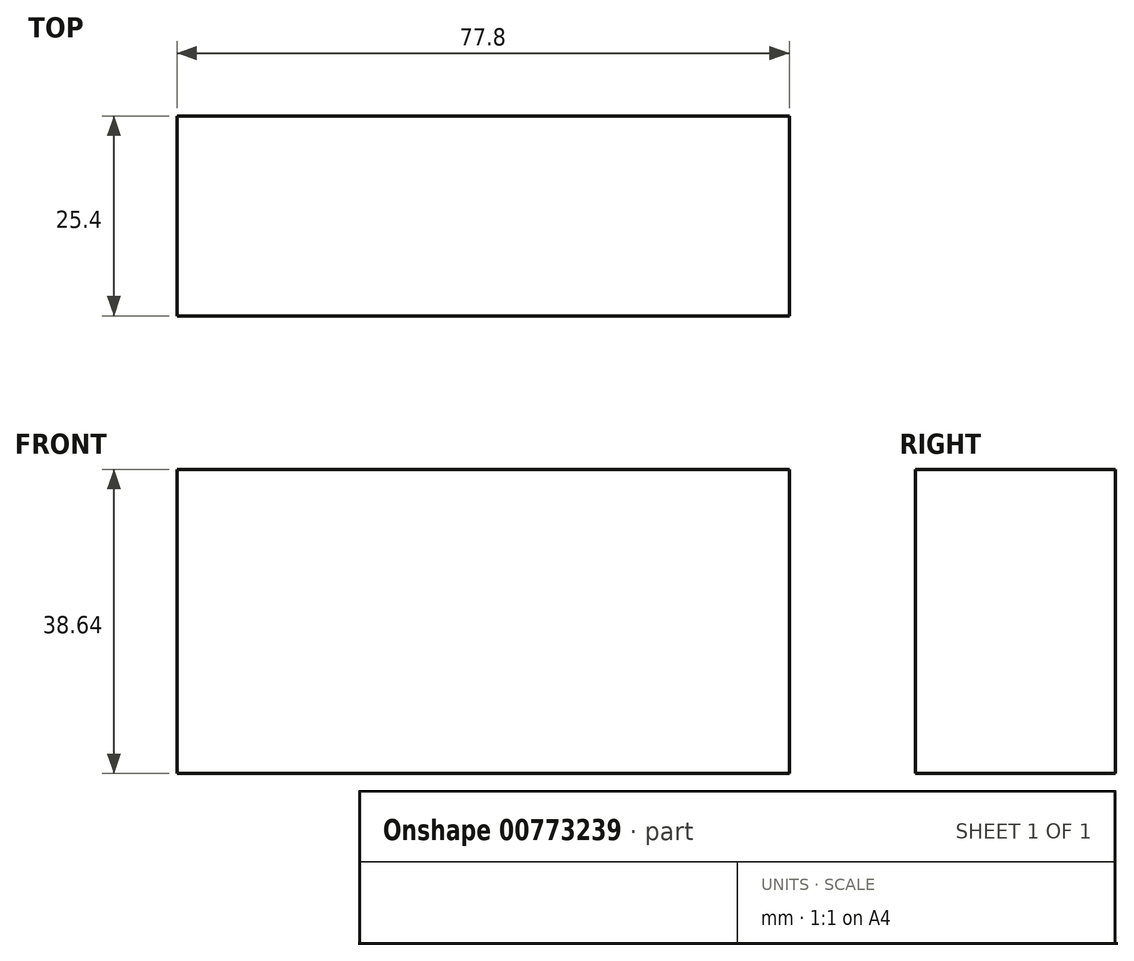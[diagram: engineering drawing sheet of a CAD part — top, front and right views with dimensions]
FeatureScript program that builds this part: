
annotation { "Feature Type Name" : "Feature", "Feature Type Description" : "" }
export const myFeature = defineFeature(function(context is Context, id is Id, definition is map)
    precondition{}
    {
        {
            var Q0;
            Q0=qCreatedBy(makeId("Front.planeOp"),FACE);
            var sketch = newSketch(context, id + "F0", { "sketchPlane" : qUnion([Q0])});
            skLineSegment(sketch, "E0", {"start": v(-121.6, -27.43) * mm, "end": v(-88.16, 11.9) * mm});
            skLineSegment(sketch, "E1", {"start": v(-88.16, 11.9) * mm, "end": v(-64.26, -23.7) * mm});
            skLineSegment(sketch, "E2", {"start": v(53.7, 23.17) * mm, "end": v(105.51, -15.95) * mm});
            skSolve(sketch);
        }
        {
            var Q0;
            Q0=qCreatedBy(makeId("Top.planeOp"),FACE);
            var Q1;
            Q1=sQuery(id+"F0.wireOp",VERTEX,"E0.end");
            cPlane(context, id + "F1", {"entities" : qUnion([Q0, Q1]), "cplaneType" : CPlaneType.PLANE_POINT, "offset" : 25.4 * mm, "width" : 152.4 * mm, "height" : 152.4 * mm});
        }
        {
            var Q0;
            Q0=qCreatedBy(makeId("Front.planeOp"),FACE);
            var sketch = newSketch(context, id + "F2", { "sketchPlane" : qUnion([Q0])});
            skLineSegment(sketch, "E3.bottom", {"start": v(-33.75, -75.87) * mm, "end": v(44.05, -75.87) * mm});
            skLineSegment(sketch, "E3.top", {"start": v(-33.75, -37.23) * mm, "end": v(44.05, -37.23) * mm});
            skLineSegment(sketch, "E3.left", {"start": v(-33.75, -75.87) * mm, "end": v(-33.75, -37.23) * mm});
            skLineSegment(sketch, "E3.right", {"start": v(44.05, -75.87) * mm, "end": v(44.05, -37.23) * mm});
            skSolve(sketch);
        }
        {
            var Q0;
            Q0=makeQuery(id+"F2.imprint","IMPRINT",FACE,{"disambiguationData":[TD([[makeQuery(id+"F2.imprint","IMPRINT",EDGE,{"derivedFrom":sQuery(id+"F2.wireOp",EDGE,"E3.bottom")}),1.0]])]});
            extrude(context, id + "F3", {"entities" : qUnion([Q0]), "depth" : 25.4 * mm, "offsetDistance" : 25.4 * mm});
        }
    });
